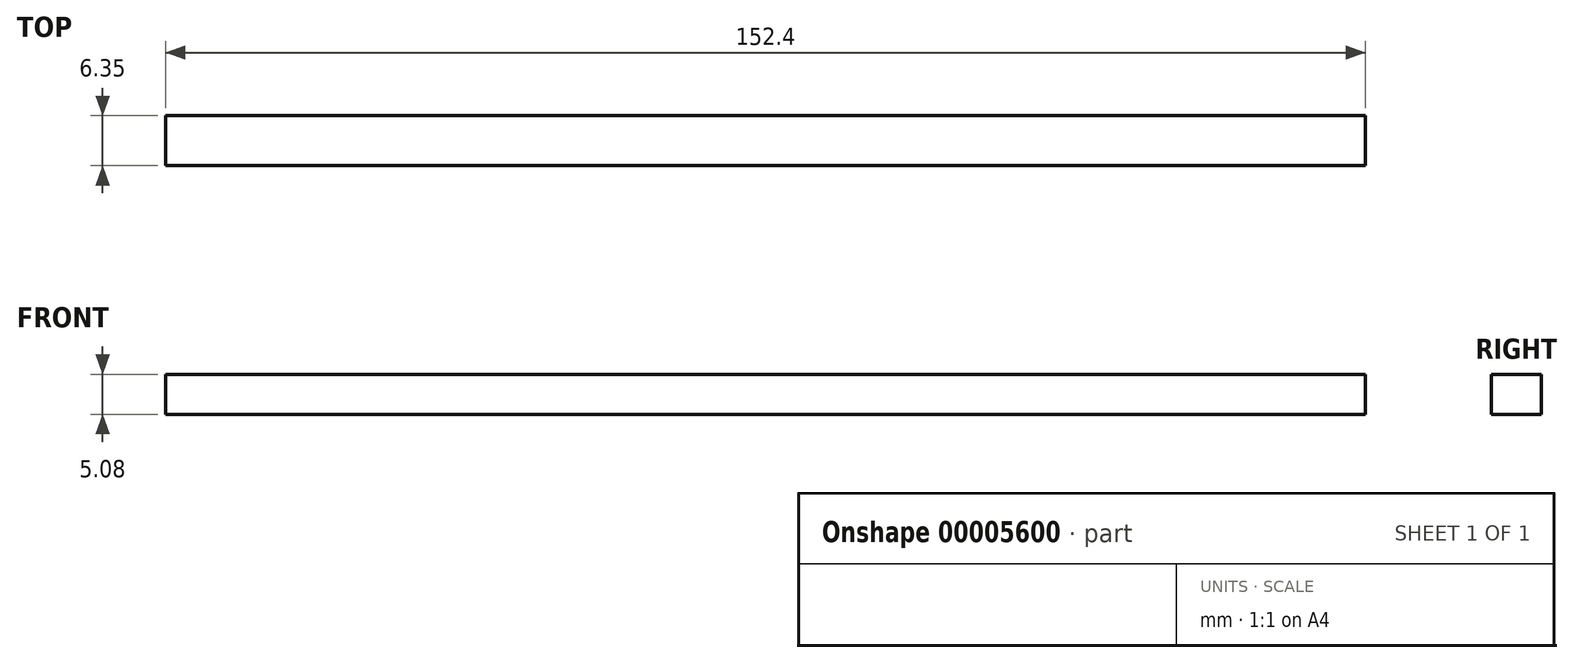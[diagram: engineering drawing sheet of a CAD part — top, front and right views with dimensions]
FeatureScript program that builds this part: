
annotation { "Feature Type Name" : "Feature", "Feature Type Description" : "" }
export const myFeature = defineFeature(function(context is Context, id is Id, definition is map)
    precondition{}
    {
        {
            var Q0;
            Q0=qCreatedBy(makeId("Top.planeOp"),FACE);
            var sketch = newSketch(context, id + "F0", { "sketchPlane" : qUnion([Q0])});
            skLineSegment(sketch, "E0.bottom", {"start": v(-68.83, 0) * mm, "end": v(83.57, 0) * mm});
            skLineSegment(sketch, "E0.top", {"start": v(-68.83, 6.35) * mm, "end": v(83.57, 6.35) * mm});
            skLineSegment(sketch, "E0.left", {"start": v(-68.83, 0) * mm, "end": v(-68.83, 6.35) * mm});
            skLineSegment(sketch, "E0.right", {"start": v(83.57, 0) * mm, "end": v(83.57, 6.35) * mm});
            skFitSpline(sketch, "E1", {"points": [v(-68.83, 6.35) * mm, v(-9.58, 26.7) * mm, v(27.85, 71.6) * mm, v(36.42, 16.79) * mm, v(69.76, 38.26) * mm], "startDerivative": vector(229.53, 13.96) * mm, "endDerivative": vector(191.03, 204.47) * mm});
            skSolve(sketch);
        }
        {
            var Q0;
            Q0 = qSketchRegion(id + "F0", true);
            extrude(context, id + "F1", {"entities" : qUnion([Q0]), "endBound" : BoundingType.SYMMETRIC, "depth" : 5.08 * mm});
        }
    });
